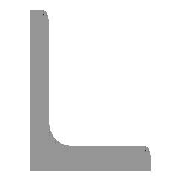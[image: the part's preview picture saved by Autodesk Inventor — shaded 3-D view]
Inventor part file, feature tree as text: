
AUTODESK INVENTOR PART (.ipt)
format: ipt  version: 2016 (Build 200138000, 138)  size: 131,584 bytes
history: native  units: mm (DEFAULTED — no unit token found)
features: other x4, sketch x3, extrude x2, plane x2
ambient origin geometry x8: Origin, YZ Plane, XZ Plane, XY Plane, X Axis, Y Axis, Z Axis, Center Point
bodies: Solid1 (feature_tree)
feature tree (11):
  parser-record x1  (decoder bookkeeping rows leaked as tree rows — omitted from the tree; the rows remain in map.json)
  other  "Driven Length"
  other  "Plano inicial"
  other  "Plano final"
  extrude  "Cuerpo"  Depth=38.1mm
  sketch  "Boceto5"  dims[d4=2400.0mm d5=0.0mm d10=0.0mm d11=0.0mm d12=-0.0mm d13=2400.0mm d14=4.826mm d15=2.286mm d16=90.0deg d17=2400.0mm d18=10.0mm d19=0.0mm]
  plane  "Plano de trabajo4"
  extrude  "Extrusión2"  Depth=4.7625mm
  sketch  "Sketch3"  dims[d0=38.1mm d1=38.1mm]
  plane  "Work Plane3"
  sketch  "Sketch4"  dims[d2=4.7625mm d3=4.7625mm]
